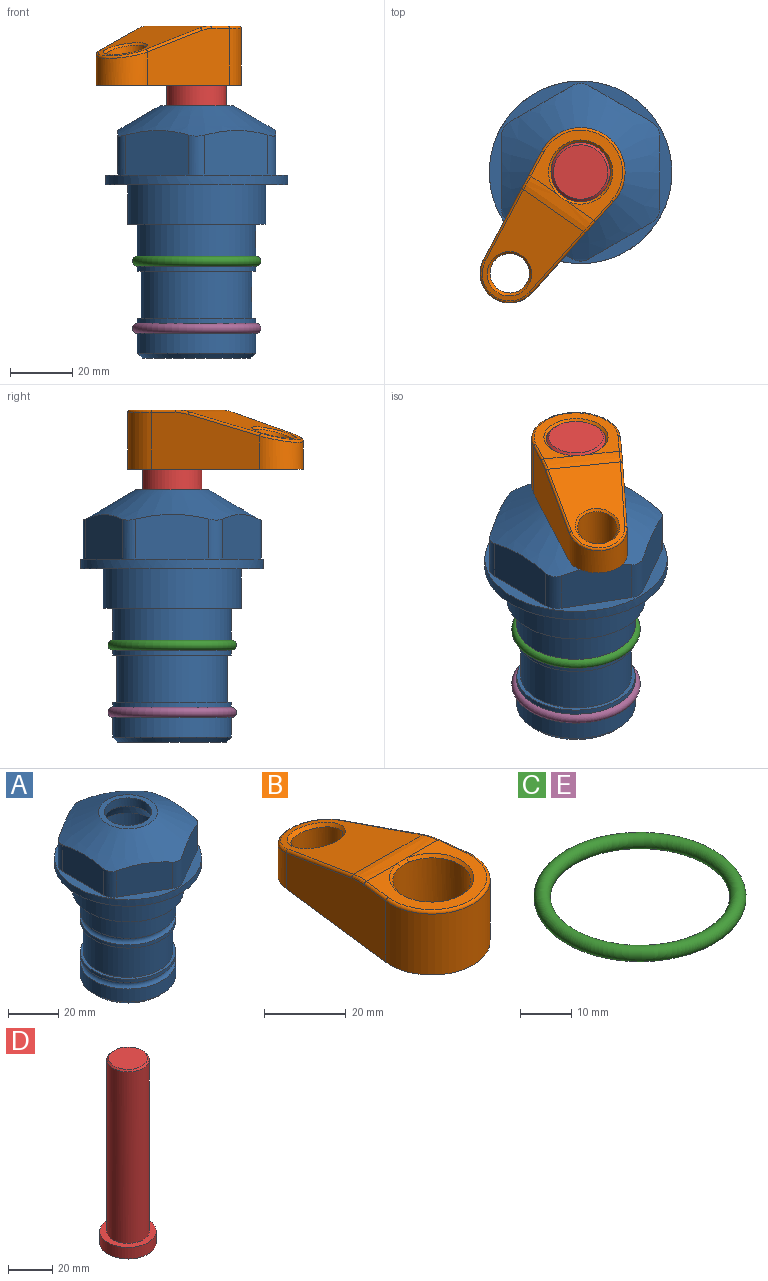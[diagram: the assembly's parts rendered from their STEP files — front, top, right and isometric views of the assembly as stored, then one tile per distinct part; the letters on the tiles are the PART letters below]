
ASSEMBLY  parts=5 mates=4
PART A: 36 faces, bbox 58.7x58.7x81 mm
  f0: cylinder r=17.78mm len=35.56mm, axis (0,0,1), area 1670.8mm2, adj f23,f24,f31
  f1: cylinder r=19.05mm len=38.1mm, axis (0,0,1), area 1191.9mm2, adj f26,f27,f30
  f2: plane 58.66x58.66mm, normal (0,0,-1), area 1150.6mm2, adj f3,f28
  f3: cylinder r=29.33mm len=58.66mm, axis (0,0,-1), area 585.1mm2, adj f2,f4
  f4: plane 58.66x58.66mm, normal (0,0,1), area 475.9mm2, adj f3,f5,f6,f7,f8,f9,f10,f11
  f5: plane 20.32x14.34mm, normal (-0.5,0.87,0), area 324.4mm2, adj f4,f15,f16,f17
  f6: plane 20.32x14.34mm, normal (0.5,0.87,0), area 324.4mm2, adj f4,f14,f15,f17
  f7: plane 23.48x14.34mm, normal (1,0,0), area 324.4mm2, adj f4,f13,f14,f17
  f8: plane 20.32x14.34mm, normal (0.5,-0.87,0), area 324.4mm2, adj f4,f12,f13,f17
  f9: plane 20.32x14.34mm, normal (-0.5,-0.87,0), area 324.4mm2, adj f4,f11,f12,f17
  f10: plane 23.48x14.34mm, normal (-1,0,0), area 324.4mm2, adj f4,f11,f16,f17
  f11: cylinder r=5.08mm len=12.85mm, axis (0,0,-1), area 67.2mm2, adj f4,f9,f10,f17
  f12: cylinder r=5.08mm len=12.85mm, axis (0,0,-1), area 67.2mm2, adj f4,f8,f9,f17
  f13: cylinder r=5.08mm len=12.85mm, axis (0,0,-1), area 67.2mm2, adj f4,f7,f8,f17
  f14: cylinder r=5.08mm len=12.85mm, axis (0,0,-1), area 67.2mm2, adj f4,f6,f7,f17
  f15: cylinder r=5.08mm len=12.85mm, axis (0,0,-1), area 67.2mm2, adj f4,f5,f6,f17
  f16: cylinder r=5.08mm len=12.85mm, axis (0,0,-1), area 67.2mm2, adj f4,f5,f10,f17
  f17: cone r=11.73mm half-angle=60deg, axis (0,0,-1), area 2071.8mm2, adj f5,f6,f7,f8,f9,f10,f11,f12
  f18: plane 23.46x23.46mm, normal (0,0,1), area 147.4mm2, adj f17,f35
  f19: plane 34.93x34.93mm, normal (0,0,-1), area 958mm2, adj f29
  f20: cylinder r=19.05mm len=38.1mm, axis (0,0,1), area 760.1mm2, adj f21,f29
  f21: torus R=19.05mm, axis (0,0,1), area 565.3mm2, adj f20,f22
  f22: cylinder r=19.05mm len=38.1mm, axis (0,0,1), area 190mm2, adj f21,f23
  f23: plane 38.1x38.1mm, normal (0,0,1), area 146.9mm2, adj f0,f22
  f24: plane 38.1x38.1mm, normal (0,0,-1), area 146.9mm2, adj f0,f25
  f25: cylinder r=19.05mm len=38.1mm, axis (0,0,1), area 190mm2, adj f24,f26
  f26: torus R=19.05mm, axis (0,0,1), area 565.3mm2, adj f1,f25
  f27: plane 44.45x44.45mm, normal (0,0,-1), area 411.7mm2, adj f1,f28
  f28: cylinder r=22.23mm len=44.45mm, axis (0,0,1), area 1773.5mm2, adj f2,f27
  f29: cone r=19.05mm half-angle=45deg, axis (0,0,1), area 257.5mm2, adj f19,f20
  f30: cylinder r=3.17mm len=6.75mm, axis (-1,0,0), area 128mm2, adj f1,f33
  f31: cylinder r=3.17mm len=6.35mm, axis (-1,0,0), area 102.5mm2, adj f0,f33
  f32: plane 25.4x25.4mm, normal (0,0,1), area 506.7mm2, adj f33
  f33: cylinder r=12.7mm len=66.42mm, axis (0,0,-1), area 5236.2mm2, adj f30,f31,f32,f34
  f34: cone r=9.53mm half-angle=30deg, axis (0,0,-1), area 443.4mm2, adj f33,f35
  f35: cylinder r=9.53mm len=19.05mm, axis (0,0,-1), area 240.9mm2, adj f18,f34
PART B: 31 faces, bbox 31.7x65.5x19.8 mm
  f0: plane 39.12x18.26mm, normal (0.99,0.12,0), area 612.2mm2, adj f1,f4,f7,f11,f13,f15
  f1: cylinder r=9.53mm len=18.91mm, axis (0,0,-1), area 296.1mm2, adj f0,f2,f7,f17
  f2: plane 39.12x18.26mm, normal (-0.99,0.12,0), area 612.2mm2, adj f1,f4,f7,f12,f14,f16
  f3: cylinder r=6.35mm len=12.7mm, axis (0,0,-1), area 362.4mm2, adj f7,f18
  f4: cylinder r=14.29mm len=28.58mm, axis (0,0,-1), area 882.2mm2, adj f0,f2,f7,f10
  f5: cylinder r=9.53mm len=19.05mm, axis (0,0,-1), area 1092.6mm2, adj f7,f19,f20
  f6: plane 26.99x23.69mm, normal (0,0,1), area 216.2mm2, adj f9,f10,f11,f12,f19
  f7: plane 63.5x28.58mm, normal (0,0,-1), area 661.8mm2, adj f0,f1,f2,f3,f4,f5,f22,f23
  f8: plane 33.52x23.6mm, normal (0,0.26,0.97), area 486mm2, adj f9,f15,f16,f17,f18
  f9: cylinder r=19.05mm len=24.72mm, axis (1,0,0), area 120.4mm2, adj f6,f8,f13,f14,f20
  f10: torus R=13.49mm, axis (0,0,1), area 59mm2, adj f4,f6,f11,f12
  f11: cylinder r=0.79mm len=8.67mm, axis (0.12,-0.99,0), area 10.8mm2, adj f0,f6,f10,f13
  f12: cylinder r=0.79mm len=8.67mm, axis (0.12,0.99,0), area 10.8mm2, adj f2,f6,f10,f14
  f13: bspline ~4.95x1.42mm, area 6.1mm2, adj f0,f9,f11,f15
  f14: bspline ~4.95x1.42mm, area 6.1mm2, adj f2,f9,f12,f16
  f15: cylinder r=0.79mm len=25.95mm, axis (0.12,-0.96,0.26), area 32.9mm2, adj f0,f8,f13,f17
  f16: cylinder r=0.79mm len=25.95mm, axis (0.12,0.96,-0.26), area 32.9mm2, adj f2,f8,f14,f17
  f17: bspline ~18.91x8.38mm, area 30mm2, adj f1,f8,f15,f16
  f18: bspline ~14.29x14.29mm, area 48.3mm2, adj f3,f8
  f19: cone r=9.53mm half-angle=45deg, axis (0,0,1), area 66.5mm2, adj f5,f6,f20
  f20: bspline ~3.22x0.96mm, area 3.5mm2, adj f5,f9,f19
  f21: plane 2.75x2.72mm, normal (0,0,-1), area 2.9mm2, adj f23,f25,f28
  f22: plane 23.05x15.88mm, normal (-0.99,-0.12,0), area 323.6mm2, adj f7,f25,f26,f27,f28,f29
  f23: plane 23.05x15.88mm, normal (0.99,-0.12,0), area 323.6mm2, adj f7,f21,f25,f27,f28,f30
  f24: cylinder r=9.53mm len=10.69mm, axis (0,0,-1), area 114.7mm2, adj f7,f27,f29,f30
  f25: cylinder r=12.7mm len=20.59mm, axis (0,0,-1), area 381.1mm2, adj f7,f21,f22,f23,f26,f28
  f26: plane 2.75x2.72mm, normal (0,0,-1), area 2.9mm2, adj f22,f25,f28
  f27: plane 19.72x18.37mm, normal (0,-0.26,-0.97), area 291.8mm2, adj f22,f23,f24,f28,f29,f30
  f28: cylinder r=15.88mm len=19.92mm, axis (1,0,0), area 54.8mm2, adj f21,f22,f23,f25,f26,f27
  f29: cylinder r=1.59mm len=11mm, axis (0,0,-1), area 34.7mm2, adj f7,f22,f24,f27
  f30: cylinder r=1.59mm len=11mm, axis (0,0,-1), area 34.7mm2, adj f7,f23,f24,f27
PART C: 1 faces, bbox 44.7x44.7x3.2 mm
  f0: torus R=19.05mm, axis (0,0,1), area 1193.9mm2
PART D: 6 faces, bbox 25.4x25.4x101.6 mm
  f0: plane 17.46x17.46mm, normal (0,0,1), area 239.5mm2, adj f5
  f1: plane 25.4x25.4mm, normal (0,0,-1), area 506.7mm2, adj f2
  f2: cylinder r=12.7mm len=25.4mm, axis (0,0,1), area 506.7mm2, adj f1,f3
  f3: plane 25.4x25.4mm, normal (0,0,1), area 221.7mm2, adj f2,f4
  f4: cylinder r=9.53mm len=94.46mm, axis (0,0,1), area 5653mm2, adj f3,f5
  f5: cone r=8.73mm half-angle=45deg, axis (0,0,-1), area 64.4mm2, adj f0,f4
PART E: same geometry as C
PLACE A at identity fixed
PLACE B rot(axis=(0,0,1),145deg) t=(0,0,-12.45)mm
PLACE C at identity
PLACE D rot(axis=(0,0,1),145deg) t=(0,0,-12.45)mm
PLACE E t=(0,0,-21.59)mm
MATE fastened C.f0 <-> A.f0  axis (0,0,1) through (0,0,-24.51)mm
MATE cylindrical D.f2 <-> A.f0  axis (0,0,-1) through (0,0,-50.55)mm
MATE fastened B.f4 <-> D.f2  axis (0,0,1) through (0,0,51.05)mm
MATE fastened E.f0 <-> A.f0  axis (0,0,1) through (0,0,-46.1)mm
